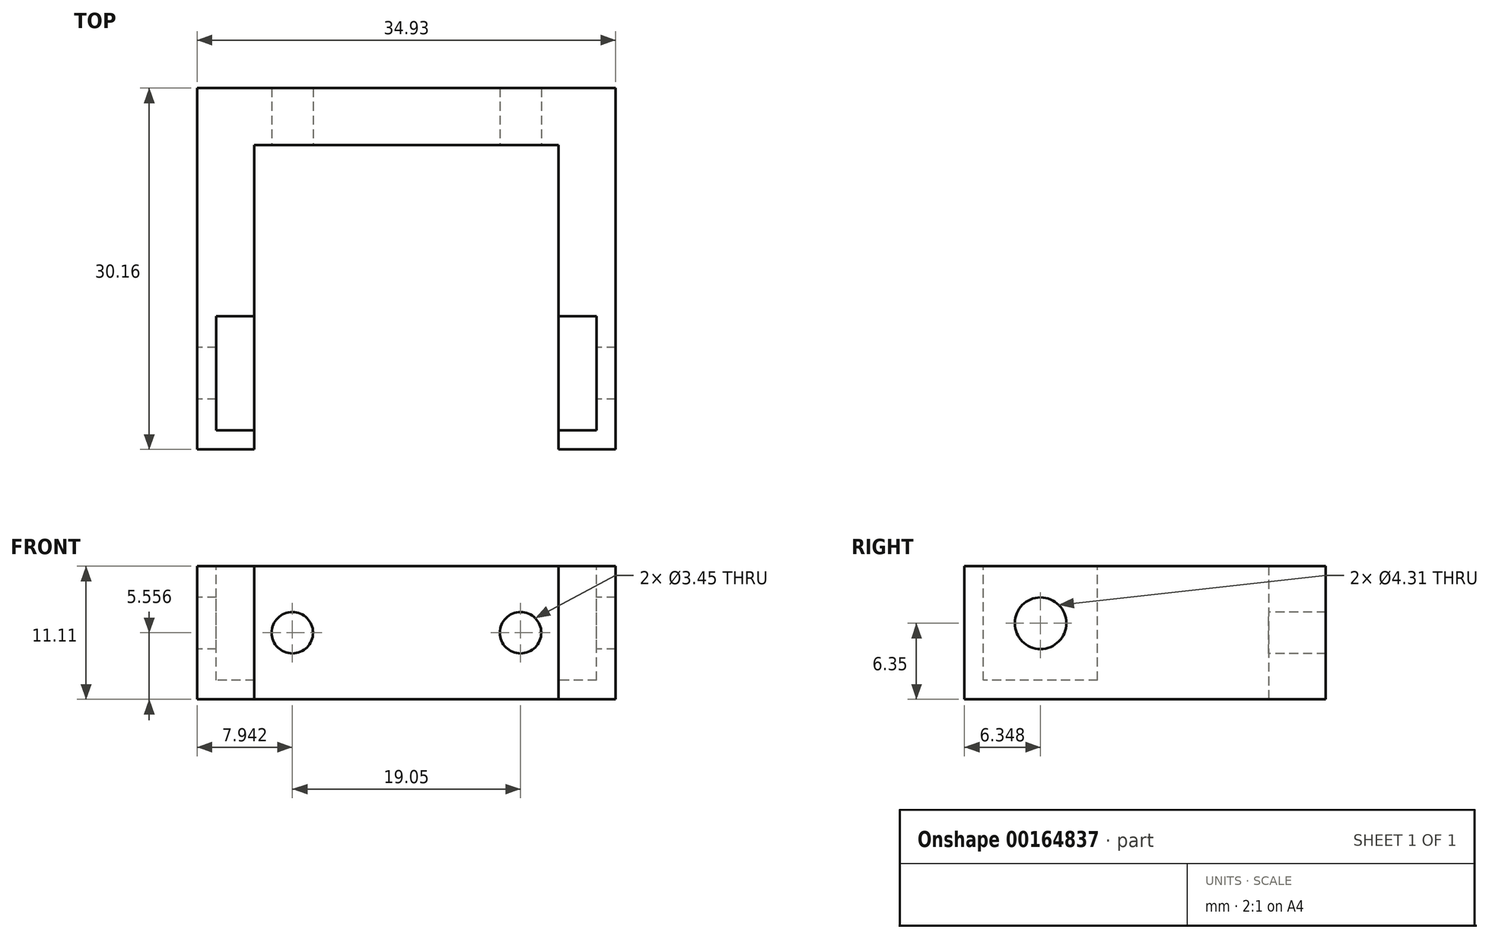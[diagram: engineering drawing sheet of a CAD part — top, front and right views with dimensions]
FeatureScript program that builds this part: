
annotation { "Feature Type Name" : "Feature", "Feature Type Description" : "" }
export const myFeature = defineFeature(function(context is Context, id is Id, definition is map)
    precondition{}
    {
        {
            var Q0;
            Q0=qCreatedBy(makeId("Top.planeOp"),FACE);
            var sketch = newSketch(context, id + "F0", { "sketchPlane" : qUnion([Q0])});
            skLineSegment(sketch, "E0.bottom", {"start": v(-34.93, 0) * mm, "end": v(0, 0) * mm});
            skLineSegment(sketch, "E0.top", {"start": v(-30.16, -4.76) * mm, "end": v(-4.76, -4.76) * mm});
            skLineSegment(sketch, "E1.top", {"start": v(-30.16, -30.16) * mm, "end": v(-34.92, -30.16) * mm});
            skLineSegment(sketch, "E1.left", {"start": v(-30.16, -4.76) * mm, "end": v(-30.16, -30.16) * mm});
            skLineSegment(sketch, "E1.right", {"start": v(-34.93, 0) * mm, "end": v(-34.93, -30.16) * mm});
            skLineSegment(sketch, "E2.top", {"start": v(-4.76, -30.16) * mm, "end": v(0, -30.16) * mm});
            skLineSegment(sketch, "E2.left", {"start": v(-4.76, -4.76) * mm, "end": v(-4.76, -30.16) * mm});
            skLineSegment(sketch, "E2.right", {"start": v(0, 0) * mm, "end": v(0, -30.16) * mm});
            skLineSegment(sketch, "E3", {"start": v(-17.46, 0) * mm, "end": v(-17.46, -4.76) * mm, "construction": true});
            skSolve(sketch);
        }
        {
            var Q0;
            Q0 = qSketchRegion(id + "F0", true);
            extrude(context, id + "F1", {"entities" : qUnion([Q0]), "depth" : 11.1 * mm});
        }
        {
            var Q0;
            Q0=makeQuery(id+"F1.opExtrude","CAP_FACE",FACE,{"disambiguationData":[OSD([sQuery(id+"F0.wireOp",EDGE,"E0.bottom"),sQuery(id+"F0.wireOp",EDGE,"E0.top"),sQuery(id+"F0.wireOp",EDGE,"E1.top"),sQuery(id+"F0.wireOp",EDGE,"E1.left"),sQuery(id+"F0.wireOp",EDGE,"E1.right"),sQuery(id+"F0.wireOp",EDGE,"E2.top"),sQuery(id+"F0.wireOp",EDGE,"E2.left"),sQuery(id+"F0.wireOp",EDGE,"E2.right")])],"isStart":false});
            var sketch = newSketch(context, id + "F2", { "sketchPlane" : qUnion([Q0])});
            skLineSegment(sketch, "E4.bottom", {"start": v(-30.16, -28.58) * mm, "end": v(-33.34, -28.58) * mm});
            skLineSegment(sketch, "E4.top", {"start": v(-30.16, -19.05) * mm, "end": v(-33.34, -19.05) * mm});
            skLineSegment(sketch, "E4.left", {"start": v(-30.16, -28.58) * mm, "end": v(-30.16, -19.05) * mm});
            skLineSegment(sketch, "E4.right", {"start": v(-33.34, -28.58) * mm, "end": v(-33.34, -19.05) * mm});
            skLineSegment(sketch, "E5", {"start": v(-33.34, -28.58) * mm, "end": v(-33.34, -30.16) * mm, "construction": true});
            skLineSegment(sketch, "E6", {"start": v(-33.34, -28.58) * mm, "end": v(-34.93, -28.58) * mm, "construction": true});
            skLineSegment(sketch, "E7.bottom", {"start": v(-1.59, -28.57) * mm, "end": v(-4.76, -28.57) * mm});
            skLineSegment(sketch, "E7.top", {"start": v(-1.59, -19.05) * mm, "end": v(-4.76, -19.05) * mm});
            skLineSegment(sketch, "E7.left", {"start": v(-1.59, -28.57) * mm, "end": v(-1.59, -19.05) * mm});
            skLineSegment(sketch, "E7.right", {"start": v(-4.76, -28.57) * mm, "end": v(-4.76, -19.05) * mm});
            skSolve(sketch);
        }
        {
            var Q0;
            Q0 = qSketchRegion(id + "F2", true);
            extrude(context, id + "F3", {"entities" : qUnion([Q0]), "operationType" : NewBodyOperationType.REMOVE, "oppositeDirection" : true, "depth" : 9.52 * mm});
        }
        {
            var Q0;
            Q0=makeQuery(id+"F1.opExtrude","SWEPT_FACE",FACE,{"disambiguationData":[OSD([sQuery(id+"F0.wireOp",EDGE,"E1.right")])]});
            var sketch = newSketch(context, id + "F4", { "sketchPlane" : qUnion([Q0])});
            skLineSegment(sketch, "E8", {"start": v(23.81, 11.11) * mm, "end": v(23.81, 1.59) * mm, "construction": true});
            skCircle(sketch, "E9", {"center": v(23.81, 6.35) * mm, "radius": 2.15 * mm});
            skSolve(sketch);
        }
        {
            var Q0;
            Q0 = qSketchRegion(id + "F4", true);
            var Q1;
            Q1=makeQuery(id+"F1.opExtrude","SWEPT_FACE",FACE,{"disambiguationData":[OSD([sQuery(id+"F0.wireOp",EDGE,"E2.right")])]});
            extrude(context, id + "F5", {"entities" : qUnion([Q0]), "operationType" : NewBodyOperationType.REMOVE, "endBound" : BoundingType.UP_TO_SURFACE, "oppositeDirection" : true, "endBoundEntityFace" : qUnion([Q1]), "depth" : 25.4 * mm});
        }
        {
            var Q0;
            Q0=makeQuery(id+"F1.opExtrude","SWEPT_FACE",FACE,{"disambiguationData":[OSD([sQuery(id+"F0.wireOp",EDGE,"E0.top")])]});
            var sketch = newSketch(context, id + "F6", { "sketchPlane" : qUnion([Q0])});
            skLineSegment(sketch, "E10.bottom", {"start": v(-4.76, 5.56) * mm, "end": v(-7.94, 5.56) * mm, "construction": true});
            skLineSegment(sketch, "E10.top", {"start": v(-4.76, 11.11) * mm, "end": v(-7.94, 11.11) * mm, "construction": true});
            skLineSegment(sketch, "E10.left", {"start": v(-4.76, 5.56) * mm, "end": v(-4.76, 11.11) * mm, "construction": true});
            skLineSegment(sketch, "E10.right", {"start": v(-7.94, 5.56) * mm, "end": v(-7.94, 11.11) * mm, "construction": true});
            skLineSegment(sketch, "E11.bottom", {"start": v(-30.16, 5.56) * mm, "end": v(-26.99, 5.56) * mm, "construction": true});
            skLineSegment(sketch, "E11.top", {"start": v(-30.16, 11.11) * mm, "end": v(-26.99, 11.11) * mm, "construction": true});
            skLineSegment(sketch, "E11.left", {"start": v(-30.16, 5.56) * mm, "end": v(-30.16, 11.11) * mm, "construction": true});
            skLineSegment(sketch, "E11.right", {"start": v(-26.99, 5.56) * mm, "end": v(-26.99, 11.11) * mm, "construction": true});
            skCircle(sketch, "E12", {"center": v(-7.94, 5.56) * mm, "radius": 1.73 * mm});
            skCircle(sketch, "E13", {"center": v(-26.99, 5.56) * mm, "radius": 1.73 * mm});
            skSolve(sketch);
        }
        {
            var Q0;
            Q0 = qSketchRegion(id + "F6", true);
            var Q1;
            Q1=makeQuery(id+"F1.opExtrude","SWEPT_FACE",FACE,{"disambiguationData":[OSD([sQuery(id+"F0.wireOp",EDGE,"E0.bottom")])]});
            extrude(context, id + "F7", {"entities" : qUnion([Q0]), "operationType" : NewBodyOperationType.REMOVE, "endBound" : BoundingType.UP_TO_SURFACE, "oppositeDirection" : true, "endBoundEntityFace" : qUnion([Q1]), "depth" : 25.4 * mm});
        }
    });
